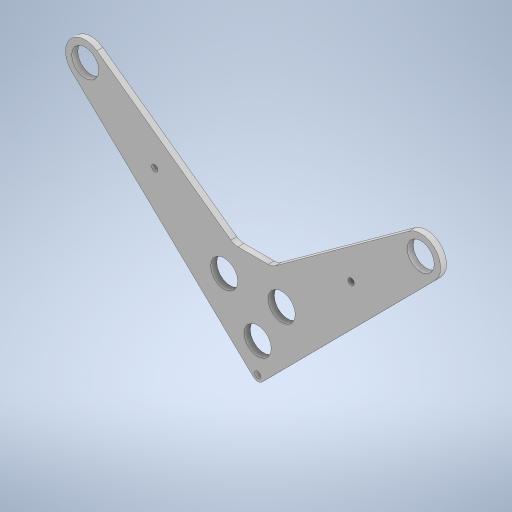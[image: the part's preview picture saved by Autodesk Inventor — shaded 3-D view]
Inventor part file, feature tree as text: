
AUTODESK INVENTOR PART (.ipt)
format: ipt  version: 2024.3 (Build 283343000, 343)  size: 301,056 bytes
history: native  units: in
note: dims shown in document units (in); Inventor stores cm internally (conversion verified against a paired STEP export)
features: extrude x1, sketch x1
ambient origin geometry x8: Origin, YZ Plane, XZ Plane, XY Plane, X Axis, Y Axis, Z Axis, Center Point
bodies: Body1 (feature_tree)
feature tree (2):
  extrude  "Extrusion2"  Depth=0.5in
  sketch  "Sketch1"  dims[d0=1.6in d1=2.4in d2=2.5in d3=1.7in d4=0.125in d5=1.13in d6=7.48in d7=4.0in d8=10.0in d9=1.13in d10=0.5in d11=0.125in d12=0.5in d13=0.5in d14=0.257in d15=0.257in d16=1.654in d19=0.25in d20=0.0in d21=0.5in d22=0.5in]
